# Revit family: QF_ELECTROLUXPROFESSIONAL_1LSN7T_WB6-27_S
name_source: partatom
category: Attrezzature speciali
units: mm (PartAtom-declared; Revit-internal decimal feet)

## family parameters
Basato su piano di lavoro = No
Condiviso = No
Punto di calcolo locali = No
Quota connettore circolare = Usa diametro
Sempre verticale = Sì
Taglio con vuoti quando caricato = No
Tipo di parte = Normale

## types (22) — shared parameters
Cold Water Maximum Pressure = 0.00 psi
Cold Water Minimum Pressure = 0.00 psi
Cold Water Size = 1"
Conn Conduit = Sì
Depth Actual = 1030 mm  [stored 3.37927 ft]
Electrical Remarks = 400 V/3N ph/50/60 Hz
Height Actual = 1620 mm
Hot Water Consumption = 0 GPM
Hot Water Maximum Pressure = 0.00 psi
Hot Water Minimum Pressure = 0.00 psi
Hot Water Size = 1"
Hot Water Temperature = -460 °F
Indirect Waste Size = 1"
Latent Heat Output = 0.0
Length Actual = 1050 mm  [stored 3.44488 ft]
Max Overcurrent Protection = 0 A
Min Ckt Ampacity = 0 A
Modello = WB6-27
Phase = 3
Produttore = Electrolux Professional
Sensible Heat Output = 0.0
URL = www.electroluxprofessional.com
Weight = 710
Weight in Pounds = 55.1
zero-valued in all types: Cold Water Connection Height, Gas KW, Hot Water Connection Height, Indirect Waste Connection Height, Prospetto di default, Steam Pounds per Hour

## per-type parameters (varying)
| type | Descrizione | Volts | Watts |
| 9890130144 | WASHER WB6-27 270L 2DOORS RIGHT/RIGHT STEAM 380-415/50/60/3 COMPASS PRO 3xWATER 13xLIQ.+POWDER SILVER EXP. | 415 V | 6200 W |
| 9890130124 | WASHER WB6-27 270L 2DOORS LEFT/LEFT STEAM 380-415/50/60/3 COMPASS PRO 2xWATER 13xLIQ. SILVER EXP. | 415 V | 6200 W |
| 9890130053 | WASHER WB6-27 270L 2DOORS RIGHT/RIGHT INDIRECT STEAM 380-415/50/60/3 2xCOMPASS PRO 3xWATER 13xLIQ. 2xDRAIN SST ALARM EXP | 415 V | 6200 W |
| 9890130033 | WASHER WB6-27 270L 2DOORS RIGHT/RIGHT DUAL STEAM+EL 380-415/50/60/3 2xCOMPASS PRO 2xWATER 13xLIQ. SILVER AIDO ALARM | 415 V | 19500 W |
| 9890130112 | WASHER WB6-27 270L 2DOORS RIGHT/RIGHT STEAM 380-415/50/60/3 2xCOMPASS PRO 2xWATER 13xLIQ.+POWDER SST AIDO IWS ALARM EXP. | 415 V | 6200 W |
| 9890130122 | WASHER WB6-27 270L 2DOORS RIGHT/RIGHT STEAM 380-415/50/60/3 COMPASS PRO 2xWATER 13xLIQ.+POWDER SILVER ALARM EXP. | 415 V | 6200 W |
| 9890130071 | WASHER WB6-27 270L 2DOORS RIGHT/RIGHT STEAM 380-415/50/60/3 2xCOMPASS PRO 2xWATER 13xLIQ. SILVER TAP | 415 V | 6200 W |
| 9890130105 | WASHER WB6-27 270L 2DOORS RIGHT/RIGHT DUAL L.STEAM+EL 380-415/50/60/3 2xCOMPASS PRO 3xWATER 13xLIQ.+POWDER SILVER AIDO | 415 V | 19500 W |
| 9890130115 | WASHER WB6-27 270L 2DOORS RIGHT/RIGHT STEAM 380-415/50/60/3 2xCOMPASS PRO 2xWATER 13xLIQ.+POWDER SST AIDO ALARM EXP. | 415 V | 6200 W |
| 9890130140 | WASHER WB6-27 270L 2DOORS RIGHT/RIGHT LOW STEAM 380-415/50/60/3 2xCOMPASS PRO 3xWATER 13xLIQ.+POWDER 2xDRAIN SILVER AIDO | 415 V | 6200 W |
| 9890130091 | WASHER WB6-27 270L 2DOORS RIGHT/RIGHT STEAM 380-415/50/60/3 2xCOMPASS PRO 3xWATER 13xLIQ.+POWDER SILVER AIDO TAP ALARM | 415 V | 6200 W |
| 9890130072 | WASHER WB6-27 270L 2DOORS RIGHT/RIGHT DUAL L.STEAM+EL 380-415/50/60/3 2xCOMPASS PRO 2xWATER 13xLIQ. SILVER AIDO ALARM | 415 V | 19500 W |
| 9890130138 | WASHER WB6-27 270L 2DOORS RIGHT/RIGHT DUAL L.STEAM+EL 380-415/50/60/3 2xCOMPASS PRO 2xWATER 13xLIQ. SILVER IWS ALARM | 415 V | 19500 W |
| 9890130077 | WASHER WB6-27 270L 2DOORS RIGHT/RIGHT LOW STEAM 380-415/50/60/3 2xCOMPASS PRO 2xWATER 13xLIQ. SILVER AIDO ALARM | 415 V | 6200 W |
| 9890130060 | WASHER WB6-27 270L 2DOORS RIGHT/RIGHT LOW STEAM 380-415/50/60/3 2xCOMPASS PRO 3xWATER 13xLIQ.+POWDER SILVER IWS ALARM | 415 V | 6200 W |
| 9890130126 | WASHER WB6-27 270L 2DOORS RIGHT/RIGHT DUAL STEAM+EL 380-415/50/60/3 2xCOMPASS PRO 3xWATER 13xLIQ.+POWDER 2xDRAIN SST AID | 415 V | 19500 W |
| 9893130004 | WASHER WB6-27 270L 2DOORS RIGHT/RIGHT STEAM 208-240/50/60/3 COMPASS PRO 2xWATER 13xLIQ.+POWDER SILVER ALARM EXP. ETL | 240 V | 6200 W |
| 9890130048 | WASHER WB6-27 270L 2DOORS RIGHT/RIGHT DUAL STEAM+EL 380-415/50/60/3 2xCOMPASS PRO 3xWATER 13xLIQ.+POWDER 2xDRAIN SILVER | 415 V | 19500 W |
| 9890130008 | WASHER WB6-27 270L 2DOORS RIGHT/RIGHT STEAM 380-415/50/60/3 COMPASS PRO 2xWATER 13xLIQ.+POWDER SILVER EXP. | 415 V | 6200 W |
| 9890130111 | WASHER WB6-27 270L 2DOORS RIGHT/RIGHT STEAM 380-415/50/60/3 COMPASS PRO 2xWATER 13xLIQ.+POWDER SST IWS ALARM EXP. | 415 V | 6200 W |
| 9890130045 | WASHER WB6-27 270L 2DOORS RIGHT/RIGHT STEAM 380-415/50/60/3 COMPASS PRO 2xWATER 13xLIQ.+POWDER SILVER EXP. | 415 V | 6200 W |
| 9890130065 | WASHER WB6-27 270L 2DOORS RIGHT/RIGHT STEAM 200/60/3 COMPASS PRO 2xWATER 13xLIQ. SST ALARM EXP. | 200 V | 6200 W |

note: [stored X ft] marks values corroborated as IEEE doubles in the binary element streams (Revit-internal decimal feet)

## geometry (parser evidence)
native form markers: Blend x4, Sweep x2
no freeform markers — native parametric forms only
